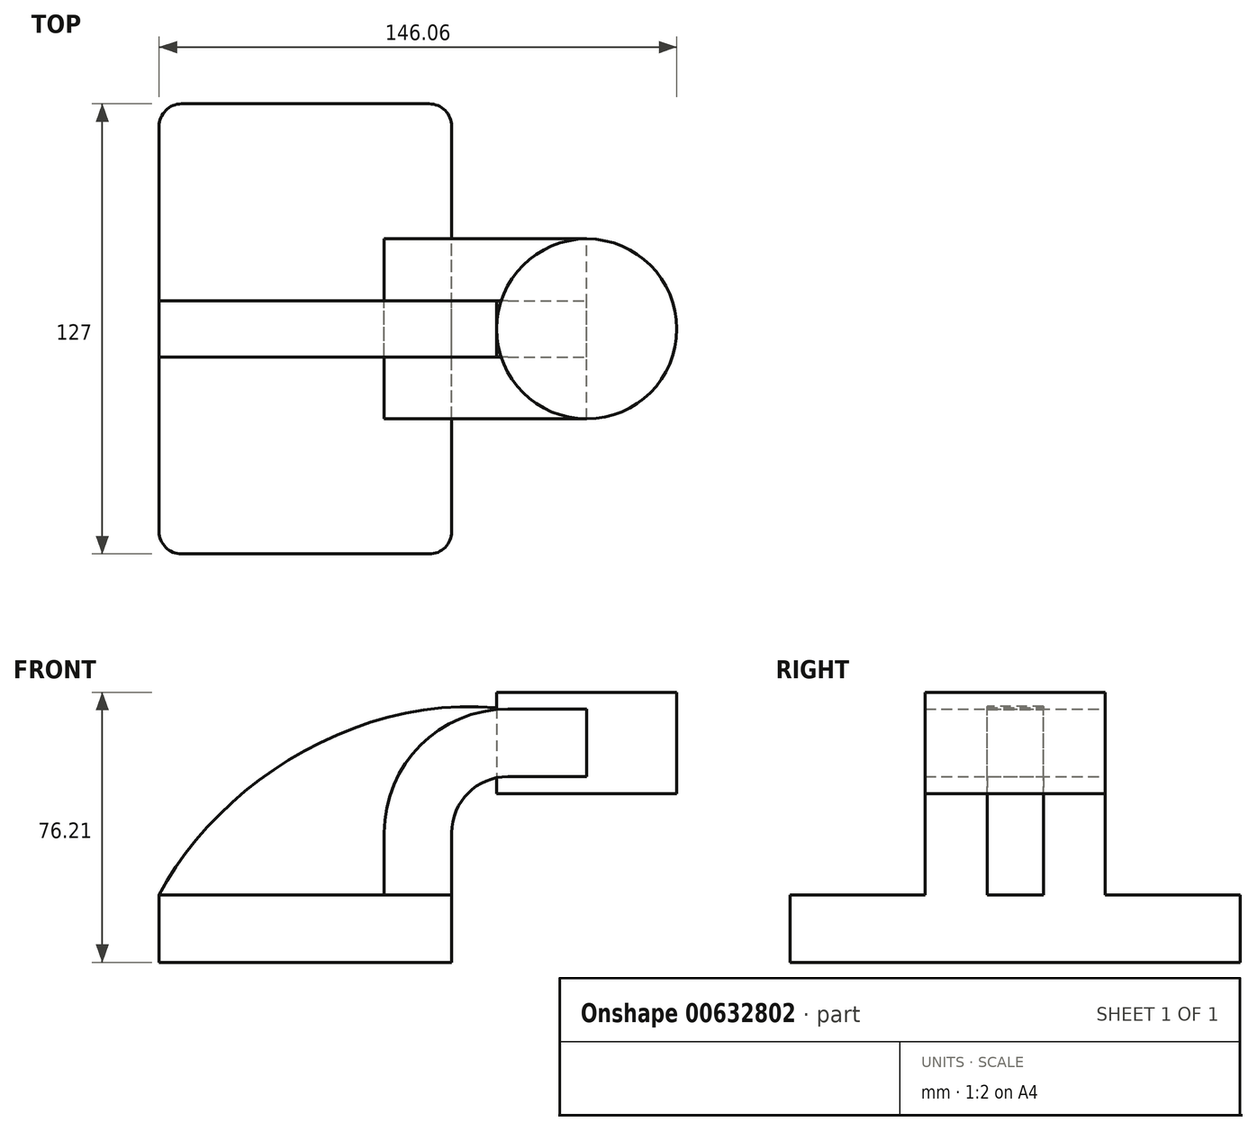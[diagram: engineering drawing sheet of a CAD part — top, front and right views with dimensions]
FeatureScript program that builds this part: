
annotation { "Feature Type Name" : "Feature", "Feature Type Description" : "" }
export const myFeature = defineFeature(function(context is Context, id is Id, definition is map)
    precondition{}
    {
        {
            var Q0;
            Q0=qCreatedBy(makeId("Front.planeOp"),FACE);
            var sketch = newSketch(context, id + "F0", { "sketchPlane" : qUnion([Q0])});
            skLineSegment(sketch, "E0.bottom", {"start": v(-41.28, 9.52) * mm, "end": v(41.27, 9.53) * mm});
            skLineSegment(sketch, "E0.top", {"start": v(-41.28, -9.52) * mm, "end": v(41.28, -9.52) * mm});
            skLineSegment(sketch, "E0.left", {"start": v(-41.28, 9.52) * mm, "end": v(-41.28, -9.53) * mm});
            skLineSegment(sketch, "E0.right", {"start": v(41.27, 9.53) * mm, "end": v(41.28, -9.52) * mm});
            skPoint(sketch, "E0.middle", {"position": v(0, 0) * mm});
            skLineSegment(sketch, "E1.bottom", {"start": v(53.97, 66.67) * mm, "end": v(104.78, 66.67) * mm});
            skLineSegment(sketch, "E1.top", {"start": v(53.97, 38.1) * mm, "end": v(104.78, 38.1) * mm});
            skLineSegment(sketch, "E1.left", {"start": v(53.97, 66.68) * mm, "end": v(53.97, 38.1) * mm});
            skLineSegment(sketch, "E1.right", {"start": v(104.78, 66.68) * mm, "end": v(104.78, 38.1) * mm});
            skPoint(sketch, "E1.middle", {"position": v(79.38, 52.39) * mm});
            skLineSegment(sketch, "E2", {"start": v(41.27, 9.53) * mm, "end": v(41.27, 27) * mm});
            skArc(sketch, "E3", {"start": v(41.27, 27) * mm, "mid": v(45.92, 38.23) * mm, "end": v(57.15, 42.88) * mm});
            skLineSegment(sketch, "E4", {"start": v(57.15, 42.88) * mm, "end": v(79.38, 42.88) * mm});
            skLineSegment(sketch, "E5.0", {"start": v(57.15, 61.93) * mm, "end": v(79.38, 61.93) * mm});
            skArc(sketch, "E5.1", {"start": v(22.22, 27) * mm, "mid": v(32.45, 51.7) * mm, "end": v(57.15, 61.93) * mm});
            skLineSegment(sketch, "E5.2", {"start": v(22.22, 9.53) * mm, "end": v(22.22, 27) * mm});
            skLineSegment(sketch, "E6", {"start": v(79.38, 38.1) * mm, "end": v(79.38, 66.68) * mm});
            skFitSpline(sketch, "E7", {"points": [v(-41.28, 9.53) * mm, v(57.15, 61.93) * mm], "startDerivative": vector(49.62, 94.55) * mm, "endDerivative": vector(122.73, -16.45) * mm});
            skSolve(sketch);
        }
        {
            var Q0;
            Q0=makeQuery(id+"F0.imprint","IMPRINT",FACE,{"disambiguationData":[TD([[makeQuery(id+"F0.imprint","IMPRINT",EDGE,{"derivedFrom":sQuery(id+"F0.wireOp",EDGE,"E0.top")}),1.0]])]});
            extrude(context, id + "F1", {"entities" : qUnion([Q0]), "endBound" : BoundingType.SYMMETRIC, "depth" : 127 * mm, "offsetDistance" : 25.4 * mm});
        }
        {
            var Q0;
            {var subQ1=sQuery(id+"F0.wireOp",EDGE,"E2");Q0=makeQuery(id+"F0.imprint","IMPRINT",FACE,{"disambiguationData":[TD([[makeQuery(id+"F0.imprint","IMPRINT",EDGE,{"derivedFrom":subQ1}),1.0]])]});}
            var Q1;
            {var subQ1=sQuery(id+"F0.wireOp",EDGE,"E4");Q1=makeQuery(id+"F0.imprint","IMPRINT",FACE,{"disambiguationData":[TD([[makeQuery(id+"F0.imprint","IMPRINT",EDGE,{"derivedFrom":subQ1}),1.0]])]});}
            extrude(context, id + "F2", {"entities" : qUnion([Q0, Q1]), "operationType" : NewBodyOperationType.ADD, "endBound" : BoundingType.SYMMETRIC, "depth" : 50.8 * mm, "offsetDistance" : 25.4 * mm});
        }
        {
            var Q0;
            Q0=makeQuery(id+"F0.imprint","IMPRINT",FACE,{"disambiguationData":[TD([[makeQuery(id+"F0.imprint","IMPRINT",EDGE,{"derivedFrom":sQuery(id+"F0.wireOp",EDGE,"E5.1")}),1.0]])]});
            var Q1;
            {var subQ0=sQuery(id+"F0.wireOp",EDGE,"E5.2");Q1=makeQuery(id+"F0.imprint","IMPRINT",FACE,{"disambiguationData":[TD([[makeQuery(id+"F0.imprint","IMPRINT",EDGE,{"derivedFrom":subQ0}),1.0]])]});}
            extrude(context, id + "F3", {"entities" : qUnion([Q0, Q1]), "endBound" : BoundingType.SYMMETRIC, "depth" : 15.88 * mm, "offsetDistance" : 25.4 * mm});
        }
        {
            var Q0;
            {var subQ4=sQuery(id+"F0.wireOp",EDGE,"E1.right");Q0=makeQuery(id+"F0.imprint","IMPRINT",FACE,{"disambiguationData":[TD([[makeQuery(id+"F0.imprint","IMPRINT",EDGE,{"derivedFrom":subQ4}),-1.0]])]});}
            var Q1;
            Q1=sQuery(id+"F0.wireOp",EDGE,"E6");
            revolve(context, id + "F4", {"entities" : qUnion([Q0]), "axis" : qUnion([Q1]), "revolveType" : RevolveType.FULL});
        }
        {
            var Q0;
            Q0=makeQuery(id+"F1.opExtrude","CAP_EDGE",EDGE,{"disambiguationData":[OSD([sQuery(id+"F0.wireOp",EDGE,"E0.right")])],"isStart":false});
            var Q1;
            Q1=makeQuery(id+"F1.opExtrude","CAP_EDGE",EDGE,{"disambiguationData":[OSD([sQuery(id+"F0.wireOp",EDGE,"E0.left")])],"isStart":false});
            var Q2;
            Q2=makeQuery(id+"F1.opExtrude","CAP_EDGE",EDGE,{"disambiguationData":[OSD([sQuery(id+"F0.wireOp",EDGE,"E0.right")])],"isStart":true});
            var Q3;
            Q3=makeQuery(id+"F1.opExtrude","CAP_EDGE",EDGE,{"disambiguationData":[OSD([sQuery(id+"F0.wireOp",EDGE,"E0.left")])],"isStart":true});
            fillet(context, id + "F5", {"entities" : qUnion([Q0, Q1, Q2, Q3]), "radius" : 6.35 * mm, "tangentPropagation" : true, "allowEdgeOverflow" : false});
        }
    });
